# Revit family: 306_be1855ee794741f2b77a34955107f5
name_source: partatom
category: Pipe Accessories
units: mm (PartAtom-declared; Revit-internal decimal feet)

## family parameters
Always vertical = Yes
Cut with Voids When Loaded = No
Part Type = Valve - Breaks Into
Round Connector Dimension = Use Diameter
Shared = No
Work Plane-Based = No

## types (3) — shared parameters
CS = Yes
Description = 3-way Change-over valve VRG233, PN10 compression fitting
L2D_Min = 3048 mm  [stored 10 ft]
MC = No
Manufacturer = ESBE
QmdConnectorList = 301;D;302;D
URL = http://www.esbe.eu
Z6 = 2 mm  [stored 0.00656168 ft]
Z6__ve = -2 mm  [stored -0.00656168 ft]
magiPartTypeId = 306
magiProductFamilyId = be1855ee794741f2b77a34955107f5

## per-type parameters (varying)
| type | A | C | CenSd_NR_6 | D | D1 | L2D | NR | W2D | X1 | X2 | X2__ve | X6 | Y0 | Y2 | Y3 | Y6 | Y7 | Y9 | Z5 | Z5__ve | Z7 | Z7__ve | magiProductId |
| VRG233 20-4.0 CPF22 | 36 mm  [stored 0.11811 ft] | 32 mm  [stored 0.104987 ft] | 11 mm | 20 mm | 50 mm  [stored 0.164042 ft] | 66 mm | 13 mm  [stored 0.0426509 ft] | 20 mm  [stored 0.0656168 ft] | 33 mm  [stored 0.108268 ft] | 7 mm  [stored 0.0229659 ft] | -7 mm | 51 mm | 10 mm  [stored 0.0328084 ft] | 10 mm  [stored 0.0328084 ft] | 19 mm | 18 mm  [stored 0.0590551 ft] | 17 mm | 16 mm | 8 mm  [stored 0.0262467 ft] | -8 mm | 28 mm | -28 mm | b59253b362d64ec59343f584c74a1e |
| VRG233 25-10 CPF28 | 41 mm  [stored 0.134514 ft] | 34 mm  [stored 0.111549 ft] | 14 mm  [stored 0.0459318 ft] | 25 mm | 52 mm  [stored 0.170604 ft] | 76 mm | 16 mm | 25 mm  [stored 0.082021 ft] | 38 mm  [stored 0.124672 ft] | 8 mm  [stored 0.0262467 ft] | -8 mm | 59 mm | 13 mm  [stored 0.0426509 ft] | 13 mm  [stored 0.0426509 ft] | 22 mm | 21 mm | 20 mm  [stored 0.0656168 ft] | 19 mm | 9 mm  [stored 0.0295276 ft] | -9 mm | 32 mm  [stored 0.104987 ft] | -32 mm  [stored -0.104987 ft] | 9dd6bf38b02e445aa00d55296c6f4f |
| VRG233 20-6.3 CPF22 | 36 mm  [stored 0.11811 ft] | 32 mm  [stored 0.104987 ft] | 11 mm | 20 mm | 50 mm  [stored 0.164042 ft] | 66 mm | 13 mm  [stored 0.0426509 ft] | 20 mm  [stored 0.0656168 ft] | 33 mm  [stored 0.108268 ft] | 7 mm  [stored 0.0229659 ft] | -7 mm | 51 mm | 10 mm  [stored 0.0328084 ft] | 10 mm  [stored 0.0328084 ft] | 19 mm | 18 mm  [stored 0.0590551 ft] | 17 mm | 16 mm | 8 mm  [stored 0.0262467 ft] | -8 mm | 28 mm | -28 mm | 5c1da628d1f94ebcb3b19e3fc0be59 |

note: column(s) folded — value = type name in every type: magiProductCode

note: [stored X ft] marks values corroborated as IEEE doubles in the binary element streams (Revit-internal decimal feet)

## geometry (parser evidence)
native form markers: Sweep x1
no freeform markers — native parametric forms only
